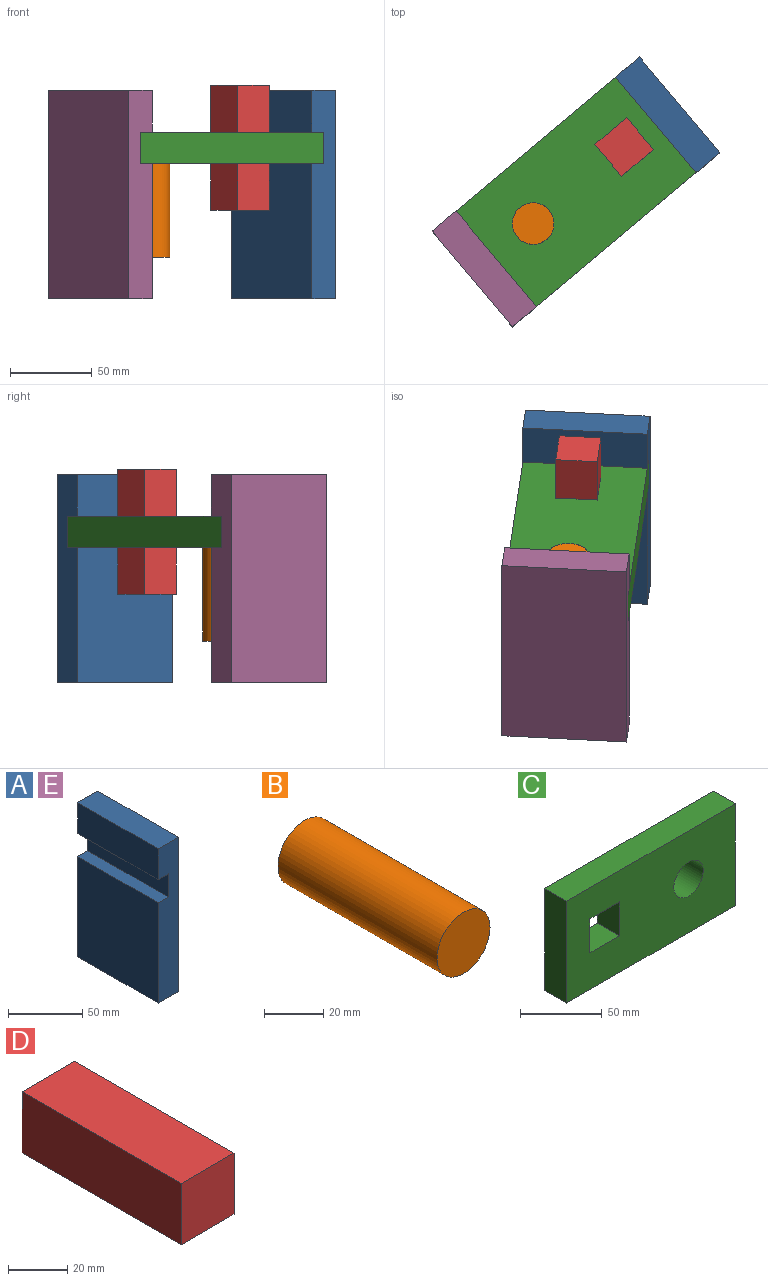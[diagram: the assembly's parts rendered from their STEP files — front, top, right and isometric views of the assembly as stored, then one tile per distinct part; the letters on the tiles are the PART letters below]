
ASSEMBLY  parts=5 mates=4
PART A: 10 faces, bbox 19.1x76.2x127 mm
  f0: plane 82.55x76.2mm, normal (-1,0,0), area 6290.3mm2, adj f1,f7,f8,f9
  f1: plane 76.2x19.05mm, normal (0,0,-1), area 1451.6mm2, adj f0,f2,f8,f9
  f2: plane 127x76.2mm, normal (1,0,0), area 9677.4mm2, adj f1,f3,f8,f9
  f3: plane 76.2x19.05mm, normal (0,0,1), area 1451.6mm2, adj f2,f4,f8,f9
  f4: plane 76.2x25.4mm, normal (-1,0,0), area 1935.5mm2, adj f3,f5,f8,f9
  f5: plane 76.2x9.53mm, normal (0,0,-1), area 725.8mm2, adj f4,f6,f8,f9
  f6: plane 76.2x19.05mm, normal (-1,0,0), area 1451.6mm2, adj f5,f7,f8,f9
  f7: plane 76.2x9.53mm, normal (0,0,1), area 725.8mm2, adj f0,f6,f8,f9
  f8: plane 127x19.05mm, normal (0,-1,0), area 2237.9mm2, adj f0,f1,f2,f3,f4,f5,f6,f7
  f9: plane 127x19.05mm, normal (0,1,0), area 2237.9mm2, adj f0,f1,f2,f3,f4,f5,f6,f7
PART B: 3 faces, bbox 25.4x76.2x25.4 mm
  f0: cylinder r=12.7mm len=76.2mm, axis (0,1,0), area 6080.5mm2, adj f1,f2
  f1: plane 25.4x25.4mm, normal (0,-1,0), area 506.7mm2, adj f0
  f2: plane 25.4x25.4mm, normal (0,1,0), area 506.7mm2, adj f0
PART C: 11 faces, bbox 146.1x19.1x76.2 mm
  f0: plane 146.05x19.05mm, normal (0,0,1), area 2782.3mm2, adj f1,f3,f4,f5
  f1: plane 76.2x19.05mm, normal (-1,0,0), area 1451.6mm2, adj f0,f2,f4,f5
  f2: plane 146.05x19.05mm, normal (0,0,-1), area 2782.3mm2, adj f1,f3,f4,f5
  f3: plane 76.2x19.05mm, normal (1,0,0), area 1451.6mm2, adj f0,f2,f4,f5
  f4: plane 146.05x76.2mm, normal (0,-1,0), area 9977.1mm2, adj f0,f1,f2,f3,f6,f7,f8,f9
  f5: plane 146.05x76.2mm, normal (0,1,0), area 9977.1mm2, adj f0,f1,f2,f3,f6,f7,f8,f9
  f6: cylinder r=12.7mm len=25.4mm, axis (0,-1,0), area 1520.1mm2, adj f4,f5
  f7: plane 25.4x19.05mm, normal (1,0,0), area 483.9mm2, adj f4,f5,f8,f10
  f8: plane 25.4x19.05mm, normal (0,0,1), area 483.9mm2, adj f4,f5,f7,f9
  f9: plane 25.4x19.05mm, normal (-1,0,0), area 483.9mm2, adj f4,f5,f8,f10
  f10: plane 25.4x19.05mm, normal (0,0,-1), area 483.9mm2, adj f4,f5,f7,f9
PART D: 6 faces, bbox 25.4x76.2x25.4 mm
  f0: plane 76.2x25.4mm, normal (-1,0,0), area 1935.2mm2, adj f1,f3,f4,f5
  f1: plane 76.2x25.4mm, normal (0,0,-1), area 1935.2mm2, adj f0,f2,f4,f5
  f2: plane 76.2x25.4mm, normal (1,0,0), area 1935.2mm2, adj f1,f3,f4,f5
  f3: plane 76.2x25.4mm, normal (0,0,1), area 1935.2mm2, adj f0,f2,f4,f5
  f4: plane 25.4x25.4mm, normal (0,-1,0), area 645mm2, adj f0,f1,f2,f3
  f5: plane 25.4x25.4mm, normal (0,1,0), area 645mm2, adj f0,f1,f2,f3
PART E: same geometry as A
PLACE A rot(axis=(0,0,1),40deg) t=(-66.02,-16.97,121.33)mm
PLACE B rot(axis=(-0.89,-0.32,0.32),96.7deg) t=(-142.99,-145.14,146.73)mm
PLACE C rot(axis=(0.25,-0.68,-0.68),152deg) t=(-113.55,-83.81,222.93)mm
PLACE D rot(axis=(0.89,0.32,0.32),96.7deg) t=(-73.84,-53.96,251.5)mm
PLACE E rot(axis=(0,0,-1),140deg) t=(-143.51,-181.47,121.33)mm
MATE planar D.f3 <-> C.f8  axis (0.64,-0.77,0) through (-67.25,-81.57,213.4)mm
MATE slider A.f6 <-> C.f1  axis (-0.77,-0.64,0) through (-48.83,-52.28,213.4)mm
MATE slider E.f6 <-> C.f3  axis (0.77,0.64,0) through (-160.71,-146.16,213.4)mm
MATE planar B.f0 <-> C.f6  axis (0,0,1) through (-130.91,-118.55,222.93)mm
